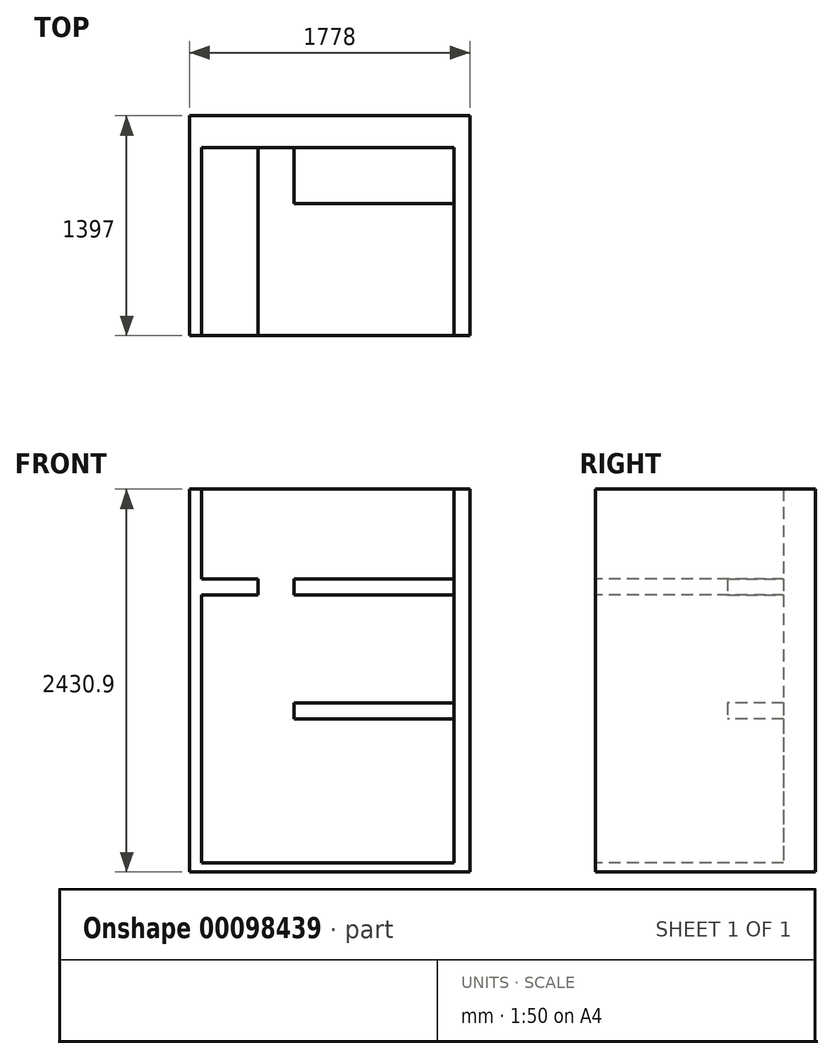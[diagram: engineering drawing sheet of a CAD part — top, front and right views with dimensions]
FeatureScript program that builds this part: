
annotation { "Feature Type Name" : "Feature", "Feature Type Description" : "" }
export const myFeature = defineFeature(function(context is Context, id is Id, definition is map)
    precondition{}
    {
        {
            var Q0;
            Q0=qCreatedBy(makeId("Top.planeOp"),FACE);
            var sketch = newSketch(context, id + "F0", { "sketchPlane" : qUnion([Q0])});
            skLineSegment(sketch, "E0.bottom", {"start": v(-799.43, -790.37) * mm, "end": v(978.57, -790.37) * mm});
            skLineSegment(sketch, "E0.top", {"start": v(-799.43, 606.63) * mm, "end": v(978.57, 606.63) * mm});
            skLineSegment(sketch, "E0.left", {"start": v(-799.43, -790.37) * mm, "end": v(-799.43, 606.63) * mm});
            skLineSegment(sketch, "E0.right", {"start": v(978.57, -790.37) * mm, "end": v(978.57, 606.63) * mm});
            skSolve(sketch);
        }
        {
            var Q0;
            Q0 = qSketchRegion(id + "F0", true);
            extrude(context, id + "F1", {"entities" : qUnion([Q0]), "depth" : 2976.48 * mm});
        }
        {
            var Q0;
            Q0=makeQuery(id+"F1.opExtrude","SWEPT_FACE",FACE,{"disambiguationData":[OSD([sQuery(id+"F0.wireOp",EDGE,"E0.bottom")])]});
            var sketch = newSketch(context, id + "F2", { "sketchPlane" : qUnion([Q0])});
            skLineSegment(sketch, "E1.bottom", {"start": v(876.97, 2976.48) * mm, "end": v(-723.23, 2976.48) * mm});
            skLineSegment(sketch, "E1.top", {"start": v(876.97, 55.48) * mm, "end": v(-723.23, 55.48) * mm});
            skLineSegment(sketch, "E1.left", {"start": v(876.97, 2976.48) * mm, "end": v(876.97, 55.48) * mm});
            skLineSegment(sketch, "E1.right", {"start": v(-723.23, 2976.48) * mm, "end": v(-723.23, 55.48) * mm});
            skSolve(sketch);
        }
        {
            var Q0;
            Q0 = qSketchRegion(id + "F2", true);
            extrude(context, id + "F3", {"entities" : qUnion([Q0]), "operationType" : NewBodyOperationType.REMOVE, "oppositeDirection" : true, "depth" : 1193.8 * mm});
        }
        {
            var Q0;
            Q0=makeQuery(id+"F3.boolean.opBoolean","COPY",FACE,{"derivedFrom":makeQuery(id+"F3.opExtrude","SWEPT_FACE",FACE,{"disambiguationData":[OSD([sQuery(id+"F2.wireOp",EDGE,"E1.top")])]})});
            var sketch = newSketch(context, id + "F4", { "sketchPlane" : qUnion([Q0])});
            skLineSegment(sketch, "E2.bottom", {"start": v(876.97, 403.43) * mm, "end": v(-139.03, 403.43) * mm});
            skLineSegment(sketch, "E2.top", {"start": v(876.97, 47.83) * mm, "end": v(-139.03, 47.83) * mm});
            skLineSegment(sketch, "E2.left", {"start": v(876.97, 403.43) * mm, "end": v(876.97, 47.83) * mm});
            skLineSegment(sketch, "E2.right", {"start": v(-139.03, 403.43) * mm, "end": v(-139.03, 47.83) * mm});
            skSolve(sketch);
        }
        {
            var Q0;
            Q0 = qSketchRegion(id + "F4", true);
            extrude(context, id + "F5", {"entities" : qUnion([Q0]), "operationType" : NewBodyOperationType.ADD, "depth" : 1016 * mm});
        }
        {
            var Q0;
            Q0=makeQuery(id+"F5.opExtrude","SWEPT_FACE",FACE,{"disambiguationData":[OSD([sQuery(id+"F4.wireOp",EDGE,"E2.top")])]});
            var sketch = newSketch(context, id + "F6", { "sketchPlane" : qUnion([Q0])});
            skLineSegment(sketch, "E3.bottom", {"start": v(876.97, 55.48) * mm, "end": v(-139.03, 55.48) * mm});
            skLineSegment(sketch, "E3.top", {"start": v(876.97, 969.88) * mm, "end": v(-139.03, 969.88) * mm});
            skLineSegment(sketch, "E3.left", {"start": v(876.97, 55.48) * mm, "end": v(876.97, 969.88) * mm});
            skLineSegment(sketch, "E3.right", {"start": v(-139.03, 55.48) * mm, "end": v(-139.03, 969.88) * mm});
            skSolve(sketch);
        }
        {
            var Q0;
            Q0 = qSketchRegion(id + "F6", true);
            extrude(context, id + "F7", {"entities" : qUnion([Q0]), "operationType" : NewBodyOperationType.REMOVE, "oppositeDirection" : true, "depth" : 355.6 * mm});
        }
        {
            var Q0;
            Q0=makeQuery(id+"F3.boolean.opBoolean","COPY",FACE,{"derivedFrom":makeQuery(id+"F3.opExtrude","SWEPT_FACE",FACE,{"disambiguationData":[OSD([sQuery(id+"F2.wireOp",EDGE,"E1.right")])]})});
            var sketch = newSketch(context, id + "F8", { "sketchPlane" : qUnion([Q0])});
            skLineSegment(sketch, "E4.bottom", {"start": v(403.43, 1858.88) * mm, "end": v(-790.37, 1858.88) * mm});
            skLineSegment(sketch, "E4.top", {"start": v(403.43, 1757.28) * mm, "end": v(-790.37, 1757.28) * mm});
            skLineSegment(sketch, "E4.left", {"start": v(403.43, 1858.88) * mm, "end": v(403.43, 1757.28) * mm});
            skLineSegment(sketch, "E4.right", {"start": v(-790.37, 1858.88) * mm, "end": v(-790.37, 1757.28) * mm});
            skSolve(sketch);
        }
        {
            var Q0;
            Q0 = qSketchRegion(id + "F8", true);
            extrude(context, id + "F9", {"entities" : qUnion([Q0]), "operationType" : NewBodyOperationType.ADD, "depth" : 355.6 * mm});
        }
        {
            var Q0;
            Q0=makeQuery(id+"F7.boolean.opBoolean","MERGE",FACE,{"derivedFrom":[makeQuery(id+"F3.boolean.opBoolean","COPY",FACE,{"derivedFrom":makeQuery(id+"F3.opExtrude","CAP_FACE",FACE,{"disambiguationData":[OSD([sQuery(id+"F2.wireOp",EDGE,"E1.bottom"),sQuery(id+"F2.wireOp",EDGE,"E1.top"),sQuery(id+"F2.wireOp",EDGE,"E1.left"),sQuery(id+"F2.wireOp",EDGE,"E1.right")])],"isStart":false})}),makeQuery(id+"F7.opExtrude","CAP_FACE",FACE,{"disambiguationData":[OSD([sQuery(id+"F6.wireOp",EDGE,"E3.bottom"),sQuery(id+"F6.wireOp",EDGE,"E3.top"),sQuery(id+"F6.wireOp",EDGE,"E3.left"),sQuery(id+"F6.wireOp",EDGE,"E3.right")])],"isStart":false})]});
            var sketch = newSketch(context, id + "F10", { "sketchPlane" : qUnion([Q0])});
            skLineSegment(sketch, "E5.bottom", {"start": v(876.97, 1858.88) * mm, "end": v(-139.03, 1858.88) * mm});
            skLineSegment(sketch, "E5.top", {"start": v(876.97, 1757.28) * mm, "end": v(-139.03, 1757.28) * mm});
            skLineSegment(sketch, "E5.left", {"start": v(876.97, 1858.88) * mm, "end": v(876.97, 1757.28) * mm});
            skLineSegment(sketch, "E5.right", {"start": v(-139.03, 1858.88) * mm, "end": v(-139.03, 1757.28) * mm});
            skSolve(sketch);
        }
        {
            var Q0;
            Q0 = qSketchRegion(id + "F10", true);
            extrude(context, id + "F11", {"entities" : qUnion([Q0]), "operationType" : NewBodyOperationType.ADD, "depth" : 355.6 * mm});
        }
        {
            var Q0;
            Q0=makeQuery(id+"F1.opExtrude","SWEPT_FACE",FACE,{"disambiguationData":[OSD([sQuery(id+"F0.wireOp",EDGE,"E0.right")])]});
            var sketch = newSketch(context, id + "F12", { "sketchPlane" : qUnion([Q0])});
            skLineSegment(sketch, "E6.bottom", {"start": v(-790.37, 2976.48) * mm, "end": v(606.63, 2976.48) * mm});
            skLineSegment(sketch, "E6.top", {"start": v(-790.37, 2430.9) * mm, "end": v(606.63, 2430.9) * mm});
            skLineSegment(sketch, "E6.left", {"start": v(-790.37, 2976.48) * mm, "end": v(-790.37, 2430.9) * mm});
            skLineSegment(sketch, "E6.right", {"start": v(606.63, 2976.48) * mm, "end": v(606.63, 2430.9) * mm});
            skSolve(sketch);
        }
        {
            var Q0;
            Q0 = qSketchRegion(id + "F12", true);
            extrude(context, id + "F13", {"entities" : qUnion([Q0]), "operationType" : NewBodyOperationType.REMOVE, "oppositeDirection" : true, "depth" : 2540 * mm});
        }
    });
